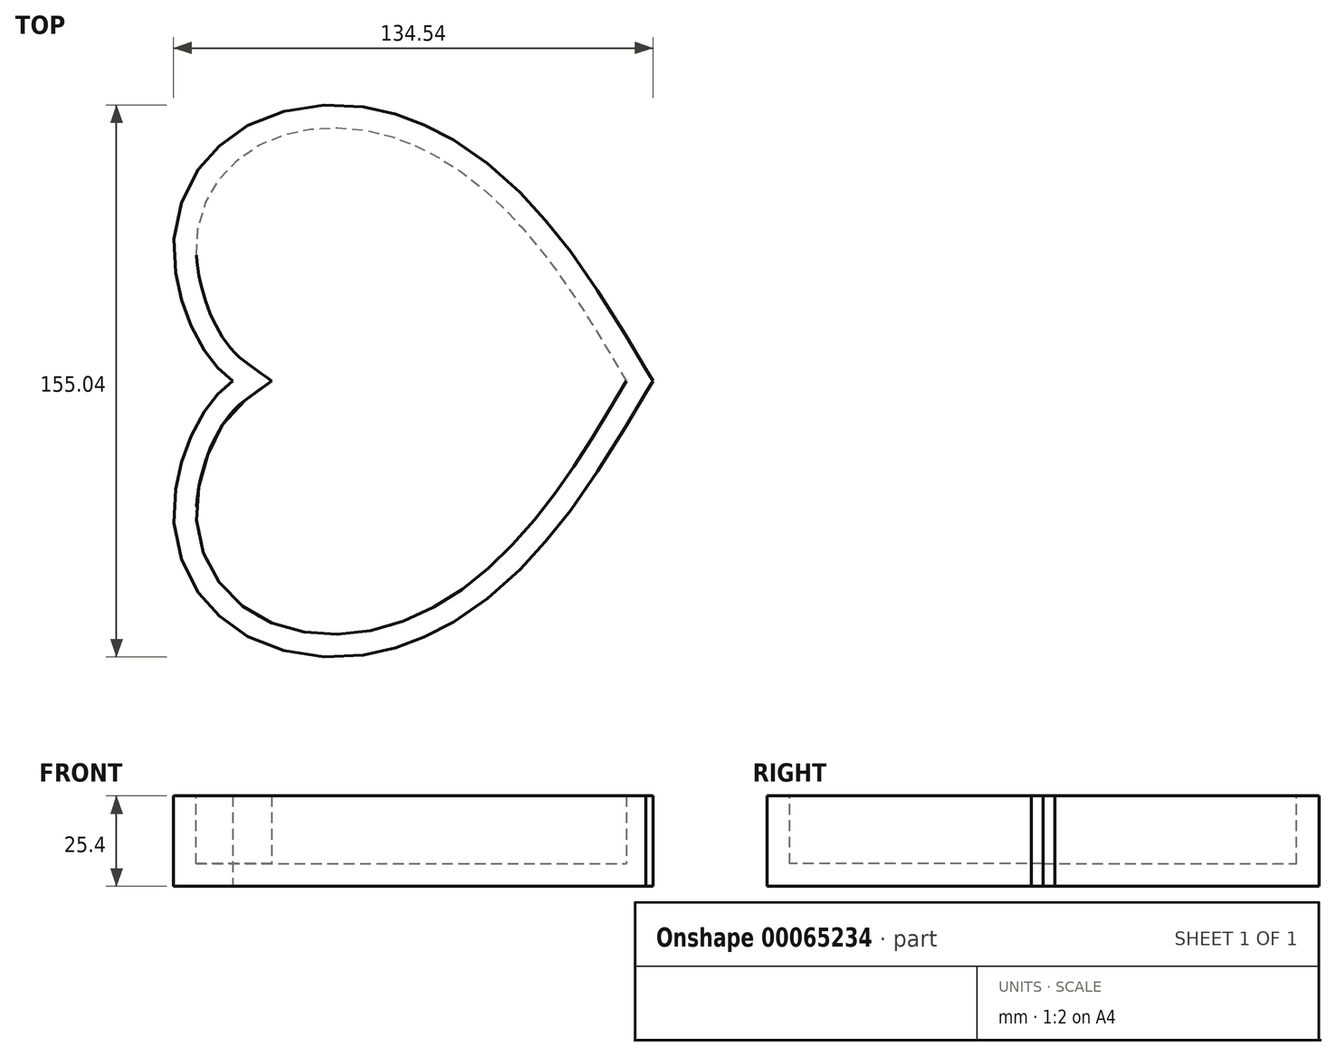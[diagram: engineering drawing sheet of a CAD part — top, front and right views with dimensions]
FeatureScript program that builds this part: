
annotation { "Feature Type Name" : "Feature", "Feature Type Description" : "" }
export const myFeature = defineFeature(function(context is Context, id is Id, definition is map)
    precondition{}
    {
        {
            var Q0;
            Q0=qCreatedBy(makeId("Top.planeOp"),FACE);
            var sketch = newSketch(context, id + "F0", { "sketchPlane" : qUnion([Q0])});
            skLineSegment(sketch, "E0.bottom", {"start": v(0, 0) * mm, "end": v(63.5, 0) * mm});
            skLineSegment(sketch, "E0.top", {"start": v(0, 88.9) * mm, "end": v(63.5, 88.9) * mm});
            skLineSegment(sketch, "E0.left", {"start": v(0, 0) * mm, "end": v(0, 88.9) * mm});
            skLineSegment(sketch, "E0.right", {"start": v(63.5, 0) * mm, "end": v(63.5, 88.9) * mm});
            skPoint(sketch, "E1", {"position": v(31.75, 88.9) * mm});
            skLineSegment(sketch, "E2", {"start": v(31.75, 88.9) * mm, "end": v(31.75, 0) * mm, "construction": true});
            skPoint(sketch, "E3", {"position": v(0, 44.45) * mm});
            skLineSegment(sketch, "E4", {"start": v(0, 44.45) * mm, "end": v(127.88, 44.45) * mm, "construction": true});
            skFitSpline(sketch, "E5", {"points": [v(0, 44.45) * mm, v(-14.67, 37.65) * mm, v(-25, 18.51) * mm, v(-25.6, 0) * mm, v(-17.3, -15.37) * mm, v(0, -25.06) * mm, v(29.02, -23.86) * mm, v(63.5, 0) * mm, v(94.1, 44.45) * mm], "startDerivative": vector(-159.03, -45.21) * mm, "endDerivative": vector(157.83, 264.87) * mm});
            skFitSpline(sketch, "E6.MirrorCS", {"points": [v(0, 44.45) * mm, v(-14.67, 51.25) * mm, v(-25, 70.39) * mm, v(-25.6, 88.9) * mm, v(-17.3, 104.27) * mm, v(0, 113.96) * mm, v(29.02, 112.76) * mm, v(63.5, 88.9) * mm, v(94.1, 44.45) * mm], "startDerivative": vector(-159.03, 45.21) * mm, "endDerivative": vector(157.83, -264.87) * mm});
            skPoint(sketch, "E7.orphan", {"position": v(63.5, 44.45) * mm});
            skFitSpline(sketch, "E8.0", {"points": [v(-1.74, 38.34) * mm, v(-3.4, 38.81) * mm, v(-6.02, 39.56) * mm, v(-9.71, 40.9) * mm, v(-12.54, 42.15) * mm, v(-14.9, 43.48) * mm, v(-16.76, 44.75) * mm, v(-18.13, 45.82) * mm, v(-19.46, 47) * mm, v(-20.7, 48.27) * mm, v(-21.87, 49.6) * mm, v(-23.33, 51.46) * mm, v(-24.98, 53.91) * mm, v(-26.72, 57) * mm, v(-28.23, 60.21) * mm, v(-29.53, 63.48) * mm, v(-30.62, 66.78) * mm, v(-31.5, 70.05) * mm, v(-32.16, 73.3) * mm, v(-32.76, 77.6) * mm, v(-32.95, 82.95) * mm, v(-32.2, 89.26) * mm, v(-30.42, 95.4) * mm, v(-27.68, 101.21) * mm, v(-24.62, 105.66) * mm, v(-21.71, 108.92) * mm, v(-18.52, 111.92) * mm, v(-14.03, 115.16) * mm, v(-7.96, 118.2) * mm, v(-1.27, 120.36) * mm, v(5.96, 121.63) * mm, v(13.62, 121.95) * mm, v(20.24, 121.36) * mm, v(25.6, 120.33) * mm, v(29.63, 119.27) * mm, v(33.66, 117.9) * mm, v(37.62, 116.26) * mm, v(41.52, 114.35) * mm, v(46.63, 111.48) * mm, v(52.84, 107.3) * mm, v(59.95, 101.5) * mm, v(65.55, 96.06) * mm, v(69.82, 91.41) * mm, v(73.93, 86.6) * mm, v(78.8, 80.3) * mm, v(84.3, 72.4) * mm, v(91.3, 61.56) * mm, v(96.26, 53.22) * mm, v(99.55, 47.7) * mm]});
            skFitSpline(sketch, "E9.0", {"points": [v(-1.74, 50.56) * mm, v(-3.4, 50.09) * mm, v(-6.02, 49.34) * mm, v(-9.71, 48) * mm, v(-12.54, 46.75) * mm, v(-14.9, 45.42) * mm, v(-16.76, 44.15) * mm, v(-18.13, 43.08) * mm, v(-19.46, 41.9) * mm, v(-20.7, 40.63) * mm, v(-21.87, 39.3) * mm, v(-23.33, 37.44) * mm, v(-24.98, 34.99) * mm, v(-26.72, 31.9) * mm, v(-28.23, 28.69) * mm, v(-29.53, 25.42) * mm, v(-30.62, 22.12) * mm, v(-31.5, 18.85) * mm, v(-32.16, 15.6) * mm, v(-32.76, 11.3) * mm, v(-32.95, 5.95) * mm, v(-32.2, -0.36) * mm, v(-30.42, -6.5) * mm, v(-27.68, -12.31) * mm, v(-24.62, -16.76) * mm, v(-21.71, -20.02) * mm, v(-18.52, -23.02) * mm, v(-14.03, -26.26) * mm, v(-7.96, -29.3) * mm, v(-1.27, -31.46) * mm, v(5.96, -32.73) * mm, v(13.62, -33.05) * mm, v(20.24, -32.46) * mm, v(25.6, -31.43) * mm, v(29.63, -30.37) * mm, v(33.66, -29) * mm, v(37.62, -27.36) * mm, v(41.52, -25.45) * mm, v(46.63, -22.58) * mm, v(52.84, -18.4) * mm, v(59.95, -12.6) * mm, v(65.55, -7.16) * mm, v(69.82, -2.51) * mm, v(73.93, 2.3) * mm, v(78.8, 8.6) * mm, v(84.3, 16.5) * mm, v(91.3, 27.34) * mm, v(96.26, 35.68) * mm, v(99.55, 41.2) * mm]});
            skLineSegment(sketch, "E10", {"start": v(99.55, 47.7) * mm, "end": v(101.57, 44.45) * mm});
            skLineSegment(sketch, "E11.MirrorCS", {"start": v(99.55, 41.2) * mm, "end": v(101.57, 44.45) * mm});
            skSolve(sketch);
        }
        {
            var Q0;
            {var subQ12=sQuery(id+"F0.wireOp",EDGE,"E10");Q0=makeQuery(id+"F0.imprint","IMPRINT",FACE,{"disambiguationData":[TD([[makeQuery(id+"F0.imprint","IMPRINT",EDGE,{"derivedFrom":subQ12}),-1.0]])]});}
            var Q1;
            {var subQ1=sQuery(id+"F0.wireOp",EDGE,"E5");var subQ3=sQuery(id+"F0.wireOp",EDGE,"E8.0");var subQ4=makeQuery(id+"F0.imprint","INTERSECT",VERTEX,{"derivedFrom":[subQ1,subQ3]});Q1=makeQuery(id+"F0.imprint","IMPRINT",FACE,{"disambiguationData":[TD([[makeQuery(id+"F0.imprint","IMPRINT",EDGE,{"disambiguationData":[TD([[subQ4,-1.0]])],"derivedFrom":subQ3}),-1.0]])]});}
            var Q2;
            {var subQ0=sQuery(id+"F0.wireOp",EDGE,"E0.top");Q2=makeQuery(id+"F0.imprint","IMPRINT",FACE,{"disambiguationData":[TD([[makeQuery(id+"F0.imprint","IMPRINT",EDGE,{"derivedFrom":subQ0}),1.0]])]});}
            var Q3;
            {var subQ3=sQuery(id+"F0.wireOp",EDGE,"E0.bottom");Q3=makeQuery(id+"F0.imprint","IMPRINT",FACE,{"disambiguationData":[TD([[makeQuery(id+"F0.imprint","IMPRINT",EDGE,{"derivedFrom":subQ3}),1.0]])]});}
            var Q4;
            {var subQ0=sQuery(id+"F0.wireOp",EDGE,"E0.bottom");Q4=makeQuery(id+"F0.imprint","IMPRINT",FACE,{"disambiguationData":[TD([[makeQuery(id+"F0.imprint","IMPRINT",EDGE,{"derivedFrom":subQ0}),-1.0]])]});}
            var Q5;
            {var subQ0=sQuery(id+"F0.wireOp",EDGE,"E0.right");Q5=makeQuery(id+"F0.imprint","IMPRINT",FACE,{"disambiguationData":[TD([[makeQuery(id+"F0.imprint","IMPRINT",EDGE,{"derivedFrom":subQ0}),-1.0]])]});}
            extrude(context, id + "F1", {"entities" : qUnion([Q0, Q1, Q2, Q3, Q4, Q5]), "depth" : 25.4 * mm});
        }
        {
            var Q0;
            Q0=makeQuery(id+"F1.opExtrude","CAP_FACE",FACE,{"disambiguationData":[OSD([sQuery(id+"F0.wireOp",EDGE,"E8.0"),sQuery(id+"F0.wireOp",EDGE,"E9.0"),sQuery(id+"F0.wireOp",EDGE,"E10"),sQuery(id+"F0.wireOp",EDGE,"E11.MirrorCS")])],"isStart":false});
            shell(context, id + "F2", {"entities" : qUnion([Q0]), "thickness" : 6.35 * mm});
        }
    });
